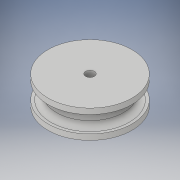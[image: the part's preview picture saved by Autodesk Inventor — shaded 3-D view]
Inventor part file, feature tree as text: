
AUTODESK INVENTOR PART (.ipt)
format: ipt  version: 2017 (Build 210142000, 142)  size: 154,112 bytes
history: native  units: in
note: dims shown in document units (in); Inventor stores cm internally (conversion verified against a paired STEP export)
features: extrude x3, sketch x3, fillet x2
ambient origin geometry x8: Origin, YZ Plane, XZ Plane, XY Plane, X Axis, Y Axis, Z Axis, Center Point
bodies: Solid1 (feature_tree)
feature tree (8):
  extrude  "Extrusion1"  Depth=0.1575in
  extrude  "Extrusion2"  Depth=0.1in
  extrude  "Extrusion3"  Depth=0.3in TaperAngle=0.0deg
  fillet  "Fillet1"  Radius=0.1575in
  fillet  "Fillet2"  Radius=1.5in
  sketch  "Sketch1"  dims[d0=1.5in d1=0.1575in]
  sketch  "Sketch2"  dims[d2=0.1in d3=0.0in d4=0.1575in]
  sketch  "Sketch3"  dims[d5=1.2in d6=0.3in d7=0.0in d8=0.1575in d9=1.5in d10=0.1in d11=0.0in d12=0.1in d13=0.1in]
